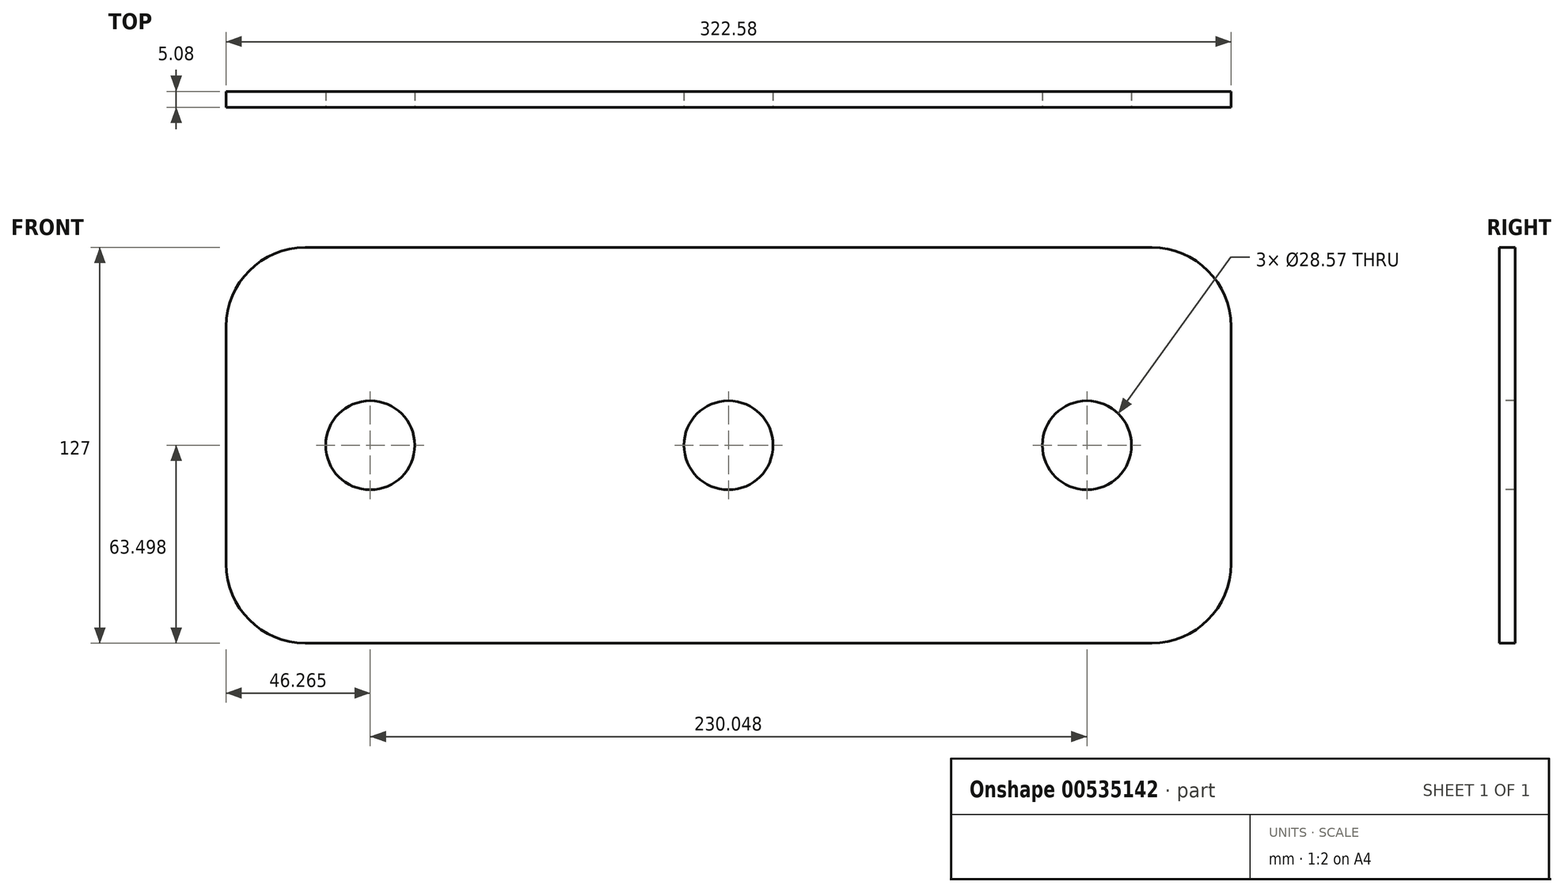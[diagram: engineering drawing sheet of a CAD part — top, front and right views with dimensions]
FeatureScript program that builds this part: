
annotation { "Feature Type Name" : "Feature", "Feature Type Description" : "" }
export const myFeature = defineFeature(function(context is Context, id is Id, definition is map)
    precondition{}
    {
        {
            var Q0;
            Q0=qCreatedBy(makeId("Front.planeOp"),FACE);
            var sketch = newSketch(context, id + "F0", { "sketchPlane" : qUnion([Q0])});
            skLineSegment(sketch, "E0.bottom", {"start": v(-221.48, 71.07) * mm, "end": v(101.1, 71.07) * mm});
            skLineSegment(sketch, "E0.top", {"start": v(-221.48, -55.93) * mm, "end": v(101.1, -55.93) * mm});
            skLineSegment(sketch, "E0.left", {"start": v(-221.48, 71.07) * mm, "end": v(-221.48, -55.93) * mm});
            skLineSegment(sketch, "E0.right", {"start": v(101.1, 71.07) * mm, "end": v(101.1, -55.93) * mm});
            skSolve(sketch);
        }
        {
            var Q0;
            Q0=makeQuery(id+"F0.imprint","IMPRINT",FACE,{"disambiguationData":[TD([[makeQuery(id+"F0.imprint","IMPRINT",EDGE,{"derivedFrom":sQuery(id+"F0.wireOp",EDGE,"E0.bottom")}),-1.0]])]});
            extrude(context, id + "F1", {"entities" : qUnion([Q0]), "depth" : 5.08 * mm});
        }
        {
            var Q0;
            Q0=makeQuery(id+"F1.opExtrude","SWEPT_EDGE",EDGE,{"disambiguationData":[OSD([sQuery(id+"F0.wireOp",EDGE,"E0.bottom"),sQuery(id+"F0.wireOp",EDGE,"E0.right")])]});
            var Q1;
            Q1=makeQuery(id+"F1.opExtrude","SWEPT_EDGE",EDGE,{"disambiguationData":[OSD([sQuery(id+"F0.wireOp",EDGE,"E0.top"),sQuery(id+"F0.wireOp",EDGE,"E0.right")])]});
            var Q2;
            Q2=makeQuery(id+"F1.opExtrude","SWEPT_EDGE",EDGE,{"disambiguationData":[OSD([sQuery(id+"F0.wireOp",EDGE,"E0.bottom"),sQuery(id+"F0.wireOp",EDGE,"E0.left")])]});
            var Q3;
            Q3=makeQuery(id+"F1.opExtrude","SWEPT_EDGE",EDGE,{"disambiguationData":[OSD([sQuery(id+"F0.wireOp",EDGE,"E0.top"),sQuery(id+"F0.wireOp",EDGE,"E0.left")])]});
            fillet(context, id + "F2", {"entities" : qUnion([Q0, Q1, Q2, Q3]), "radius" : 25.4 * mm, "tangentPropagation" : true, "allowEdgeOverflow" : false});
        }
        {
            var Q0;
            Q0=makeQuery(id+"F1.opExtrude","CAP_FACE",FACE,{"disambiguationData":[OSD([sQuery(id+"F0.wireOp",EDGE,"E0.bottom"),sQuery(id+"F0.wireOp",EDGE,"E0.top"),sQuery(id+"F0.wireOp",EDGE,"E0.left"),sQuery(id+"F0.wireOp",EDGE,"E0.right")])],"isStart":false});
            var sketch = newSketch(context, id + "F3", { "sketchPlane" : qUnion([Q0])});
            skLineSegment(sketch, "E1", {"start": v(-247.82, 7.57) * mm, "end": v(115.98, 7.57) * mm, "construction": true});
            skLineSegment(sketch, "E2", {"start": v(-60.2, 97.6) * mm, "end": v(-60.2, -75.3) * mm, "construction": true});
            skCircle(sketch, "E3", {"center": v(-175.21, 7.57) * mm, "radius": 14.29 * mm});
            skCircle(sketch, "E4", {"center": v(-60.2, 7.57) * mm, "radius": 14.29 * mm});
            skCircle(sketch, "E5", {"center": v(54.83, 7.57) * mm, "radius": 14.29 * mm});
            skSolve(sketch);
        }
        {
            var Q0;
            Q0=makeQuery(id+"F3.imprint","IMPRINT",FACE,{"disambiguationData":[TD([[makeQuery(id+"F3.imprint","IMPRINT",EDGE,{"derivedFrom":sQuery(id+"F3.wireOp",EDGE,"E4")}),1.0]])]});
            var Q1;
            Q1=makeQuery(id+"F3.imprint","IMPRINT",FACE,{"disambiguationData":[TD([[makeQuery(id+"F3.imprint","IMPRINT",EDGE,{"derivedFrom":sQuery(id+"F3.wireOp",EDGE,"E5")}),1.0]])]});
            var Q2;
            Q2=makeQuery(id+"F3.imprint","IMPRINT",FACE,{"disambiguationData":[TD([[makeQuery(id+"F3.imprint","IMPRINT",EDGE,{"derivedFrom":sQuery(id+"F3.wireOp",EDGE,"E3")}),1.0]])]});
            extrude(context, id + "F4", {"entities" : qUnion([Q0, Q1, Q2]), "operationType" : NewBodyOperationType.REMOVE, "oppositeDirection" : true, "depth" : 25.4 * mm});
        }
    });
